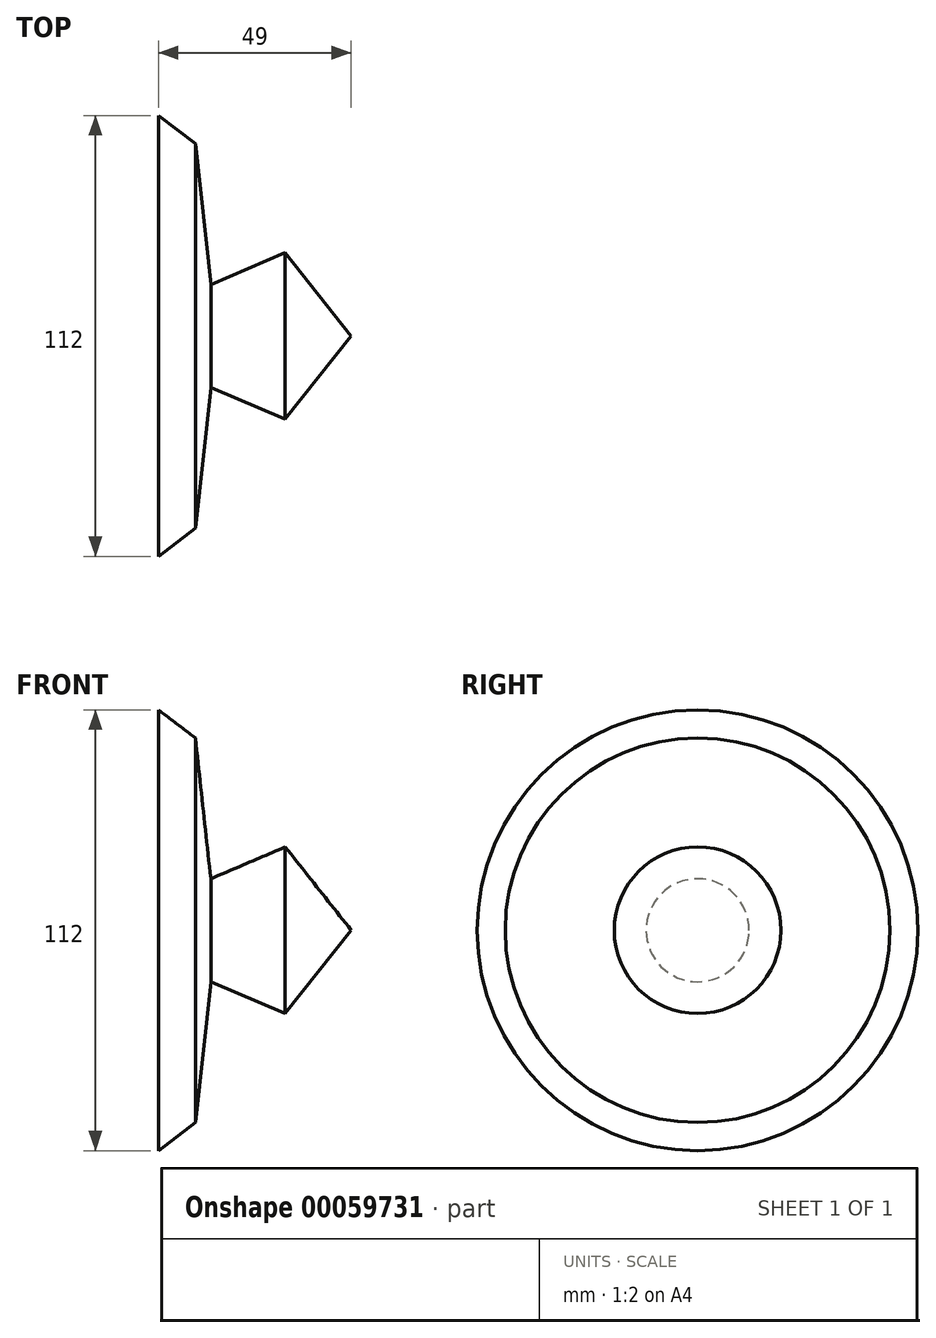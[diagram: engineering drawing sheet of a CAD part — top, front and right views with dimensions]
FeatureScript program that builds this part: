
annotation { "Feature Type Name" : "Feature", "Feature Type Description" : "" }
export const myFeature = defineFeature(function(context is Context, id is Id, definition is map)
    precondition{}
    {
        {
            var Q0;
            Q0=qCreatedBy(makeId("Front.planeOp"),FACE);
            var sketch = newSketch(context, id + "F0", { "sketchPlane" : qUnion([Q0])});
            skLineSegment(sketch, "E0", {"start": v(-49, 56) * mm, "end": v(-49, 0) * mm});
            skLineSegment(sketch, "E1", {"start": v(-49, 0) * mm, "end": v(0, 0) * mm});
            skLineSegment(sketch, "E2", {"start": v(0, 0) * mm, "end": v(-16.76, 21.17) * mm});
            skLineSegment(sketch, "E3", {"start": v(-16.76, 21.17) * mm, "end": v(-35.67, 13.08) * mm});
            skLineSegment(sketch, "E4", {"start": v(-35.67, 13.08) * mm, "end": v(-39.59, 48.87) * mm});
            skLineSegment(sketch, "E5", {"start": v(-39.59, 48.87) * mm, "end": v(-49, 56) * mm});
            skSolve(sketch);
        }
        {
            var Q0;
            Q0=makeQuery(id+"F0.imprint","IMPRINT",FACE,{"disambiguationData":[TD([[makeQuery(id+"F0.imprint","IMPRINT",EDGE,{"derivedFrom":sQuery(id+"F0.wireOp",EDGE,"E0")}),1.0]])]});
            var Q1;
            Q1=sQuery(id+"F0.wireOp",EDGE,"E1");
            revolve(context, id + "F1", {"entities" : qUnion([Q0]), "axis" : qUnion([Q1]), "revolveType" : RevolveType.FULL});
        }
    });
